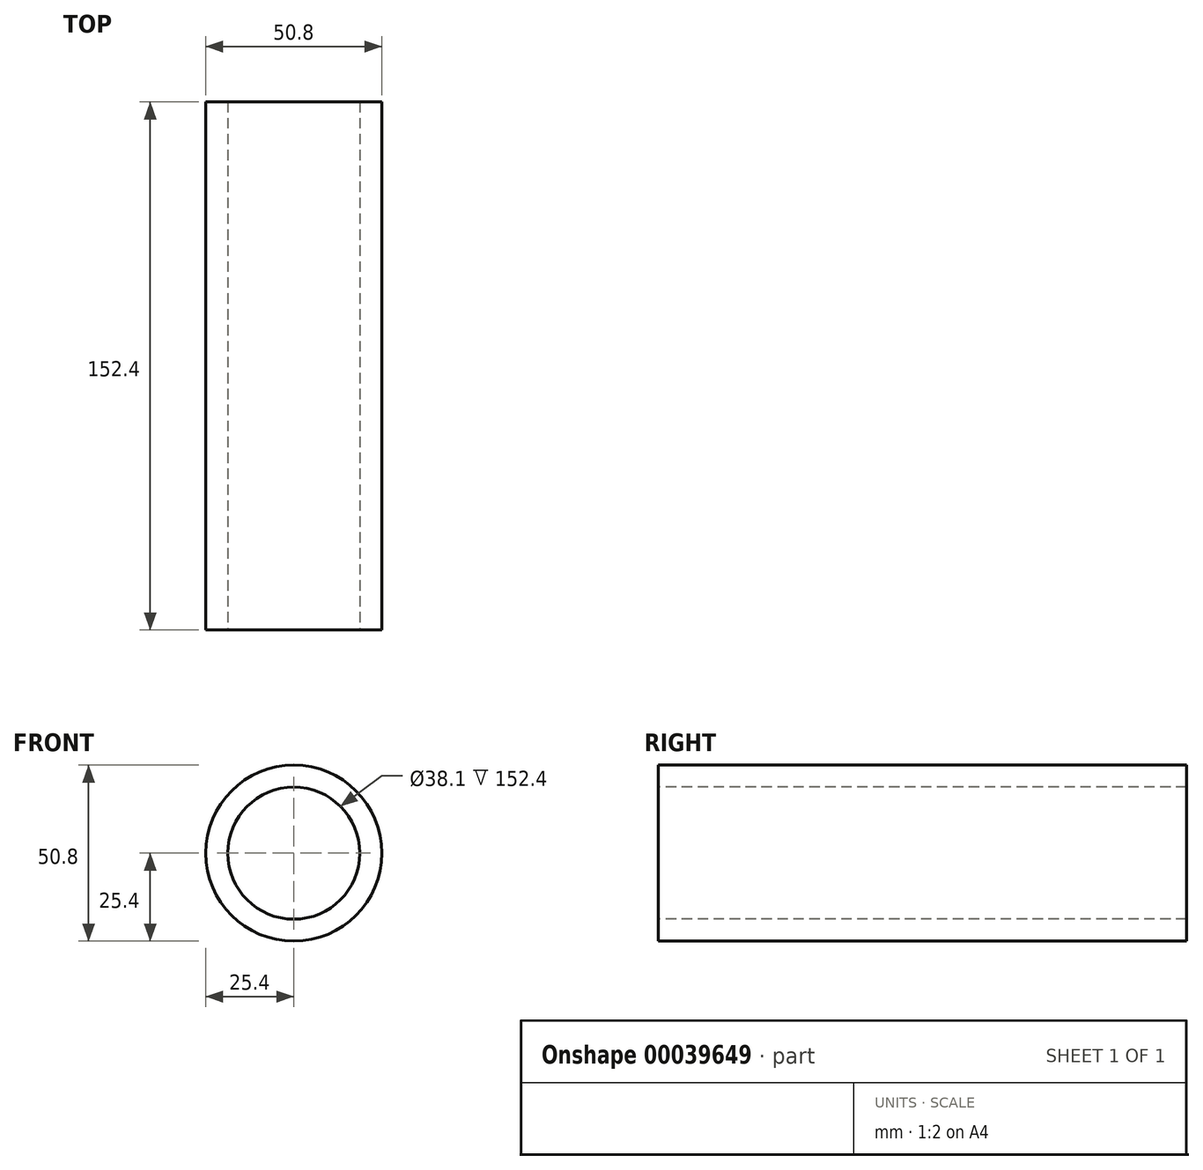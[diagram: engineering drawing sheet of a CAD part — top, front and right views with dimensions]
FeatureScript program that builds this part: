
annotation { "Feature Type Name" : "Feature", "Feature Type Description" : "" }
export const myFeature = defineFeature(function(context is Context, id is Id, definition is map)
    precondition{}
    {
        {
            var Q0;
            Q0=qCreatedBy(makeId("Top.planeOp"),FACE);
            var sketch = newSketch(context, id + "F0", { "sketchPlane" : qUnion([Q0])});
            skLineSegment(sketch, "E0", {"start": v(0, 0) * mm, "end": v(6.35, 0) * mm});
            skLineSegment(sketch, "E1", {"start": v(0, 0) * mm, "end": v(0, 152.4) * mm});
            skLineSegment(sketch, "E2", {"start": v(0, 152.4) * mm, "end": v(6.35, 152.4) * mm});
            skLineSegment(sketch, "E3", {"start": v(6.35, 152.4) * mm, "end": v(6.35, 0) * mm});
            skLineSegment(sketch, "E4", {"start": v(6.35, 0) * mm, "end": v(25.4, 0) * mm});
            skLineSegment(sketch, "E5", {"start": v(25.4, 0) * mm, "end": v(25.4, 95.33) * mm});
            skSolve(sketch);
        }
        {
            var Q0;
            Q0=makeQuery(id+"F0.imprint","IMPRINT",FACE,{"disambiguationData":[TD([[makeQuery(id+"F0.imprint","IMPRINT",EDGE,{"derivedFrom":sQuery(id+"F0.wireOp",EDGE,"E0")}),1.0]])]});
            var Q1;
            {var subQ5=sQuery(id+"F0.wireOp",EDGE,"E2");Q1=makeQuery(id+"F0.imprint","IMPRINT",FACE,{"disambiguationData":[TD([[makeQuery(id+"F0.imprint","IMPRINT",EDGE,{"derivedFrom":subQ5}),-1.0]])]});}
            var Q2;
            Q2=sQuery(id+"F0.wireOp",EDGE,"E5");
            revolve(context, id + "F1", {"entities" : qUnion([Q0, Q1]), "axis" : qUnion([Q2]), "revolveType" : RevolveType.FULL});
        }
    });
